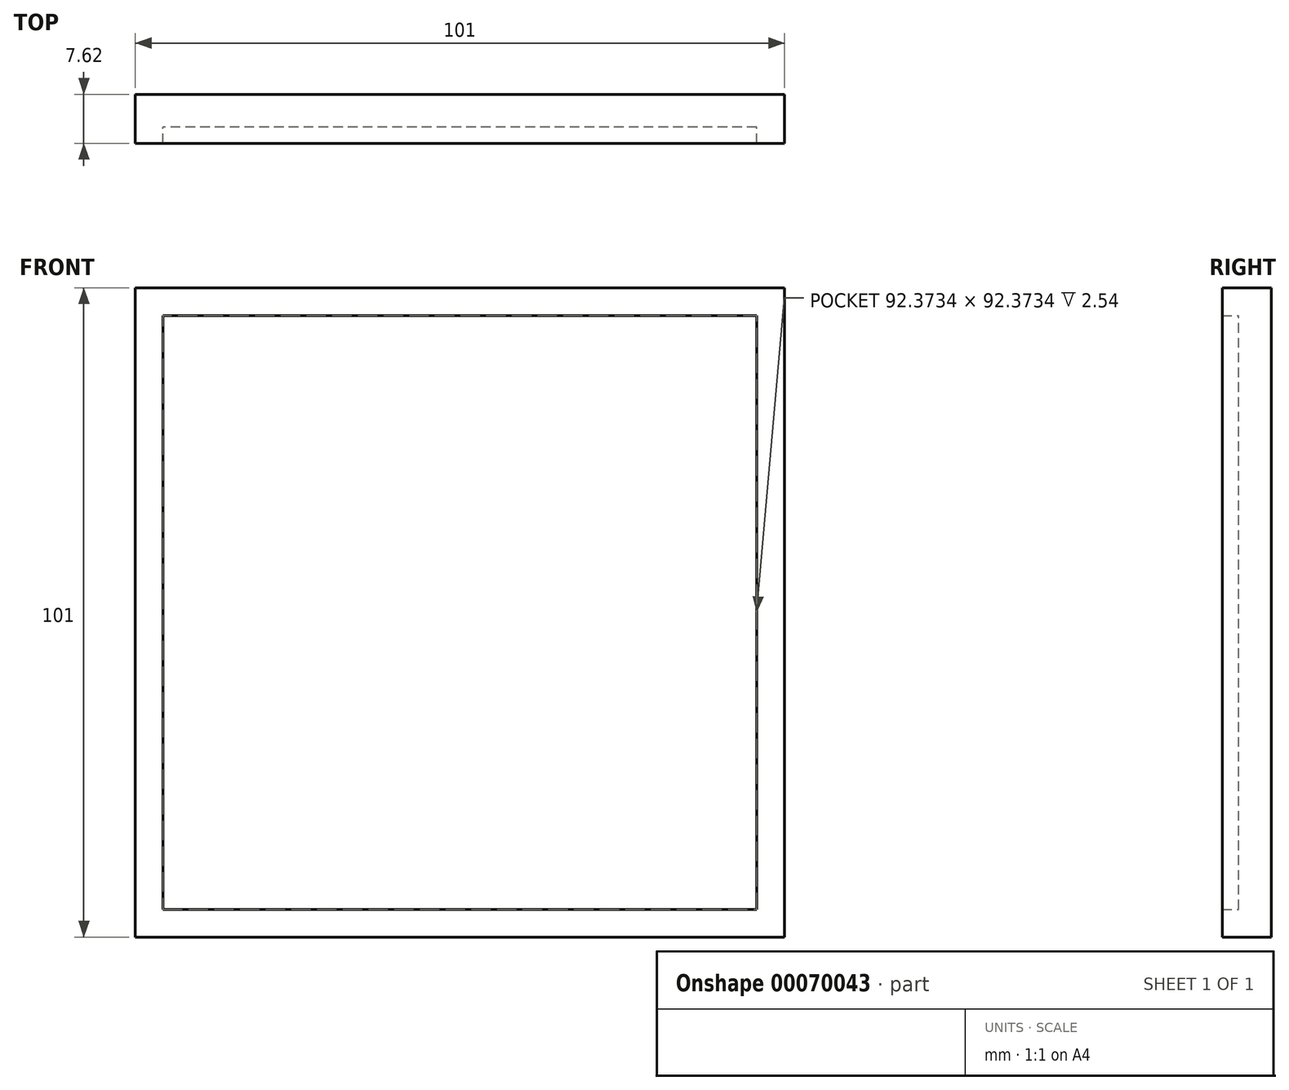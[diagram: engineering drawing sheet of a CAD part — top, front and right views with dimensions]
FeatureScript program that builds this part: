
annotation { "Feature Type Name" : "Feature", "Feature Type Description" : "" }
export const myFeature = defineFeature(function(context is Context, id is Id, definition is map)
    precondition{}
    {
        {
            var Q0;
            Q0=qCreatedBy(makeId("Front.planeOp"),FACE);
            var sketch = newSketch(context, id + "F0", { "sketchPlane" : qUnion([Q0])});
            skLineSegment(sketch, "E0.rect.bottom", {"start": v(50.8, -50.8) * mm, "end": v(-50.8, -50.8) * mm});
            skLineSegment(sketch, "E0.rect.top", {"start": v(50.8, 50.8) * mm, "end": v(-50.8, 50.8) * mm});
            skLineSegment(sketch, "E0.rect.left", {"start": v(50.8, -50.8) * mm, "end": v(50.8, 50.8) * mm});
            skLineSegment(sketch, "E0.rect.right", {"start": v(-50.8, -50.8) * mm, "end": v(-50.8, 50.8) * mm});
            skLineSegment(sketch, "E1.0", {"start": v(50.5, 50.5) * mm, "end": v(-50.5, 50.5) * mm});
            skLineSegment(sketch, "E1.1", {"start": v(50.5, -50.5) * mm, "end": v(50.5, 50.5) * mm});
            skLineSegment(sketch, "E1.2", {"start": v(50.5, -50.5) * mm, "end": v(-50.5, -50.5) * mm});
            skLineSegment(sketch, "E1.3", {"start": v(-50.5, -50.5) * mm, "end": v(-50.5, 50.5) * mm});
            skSolve(sketch);
        }
        {
            var Q0;
            Q0=makeQuery(id+"F0.imprint","IMPRINT",FACE,{"disambiguationData":[TD([[makeQuery(id+"F0.imprint","IMPRINT",EDGE,{"derivedFrom":sQuery(id+"F0.wireOp",EDGE,"E1.0")}),1.0]])]});
            extrude(context, id + "F1", {"entities" : qUnion([Q0]), "depth" : 5.08 * mm});
        }
        {
            var Q0;
            Q0=makeQuery(id+"F1.opExtrude","CAP_FACE",FACE,{"disambiguationData":[OSD([sQuery(id+"F0.wireOp",EDGE,"E1.0"),sQuery(id+"F0.wireOp",EDGE,"E1.1"),sQuery(id+"F0.wireOp",EDGE,"E1.2"),sQuery(id+"F0.wireOp",EDGE,"E1.3")])],"isStart":false});
            var sketch = newSketch(context, id + "F2", { "sketchPlane" : qUnion([Q0])});
            skLineSegment(sketch, "E2.bottom", {"start": v(46.19, -46.19) * mm, "end": v(-46.19, -46.19) * mm});
            skLineSegment(sketch, "E2.top", {"start": v(46.19, 46.19) * mm, "end": v(-46.19, 46.19) * mm});
            skLineSegment(sketch, "E2.left", {"start": v(46.19, -46.19) * mm, "end": v(46.19, 46.19) * mm});
            skLineSegment(sketch, "E2.right", {"start": v(-46.19, -46.19) * mm, "end": v(-46.19, 46.19) * mm});
            skPoint(sketch, "E2.middle", {"position": v(0, 0) * mm});
            skLineSegment(sketch, "E3.bottom", {"start": v(50.5, -50.5) * mm, "end": v(-50.5, -50.5) * mm});
            skLineSegment(sketch, "E3.top", {"start": v(50.5, 50.5) * mm, "end": v(-50.5, 50.5) * mm});
            skLineSegment(sketch, "E3.left", {"start": v(50.5, -50.5) * mm, "end": v(50.5, 50.5) * mm});
            skLineSegment(sketch, "E3.right", {"start": v(-50.5, -50.5) * mm, "end": v(-50.5, 50.5) * mm});
            skSolve(sketch);
        }
        {
            var Q0;
            Q0=makeQuery(id+"F2.imprint","IMPRINT",FACE,{"disambiguationData":[TD([[makeQuery(id+"F2.imprint","IMPRINT",EDGE,{"derivedFrom":sQuery(id+"F2.wireOp",EDGE,"E2.bottom")}),1.0]])]});
            extrude(context, id + "F3", {"entities" : qUnion([Q0]), "operationType" : NewBodyOperationType.ADD, "depth" : 2.54 * mm});
        }
        {
            var Q0;
            Q0=makeQuery(id+"F1.opExtrude","CAP_FACE",FACE,{"disambiguationData":[OSD([sQuery(id+"F0.wireOp",EDGE,"E1.0"),sQuery(id+"F0.wireOp",EDGE,"E1.1"),sQuery(id+"F0.wireOp",EDGE,"E1.2"),sQuery(id+"F0.wireOp",EDGE,"E1.3")])],"isStart":false});
            var sketch = newSketch(context, id + "F4", { "sketchPlane" : qUnion([Q0])});
            skLineSegment(sketch, "E4.bottom", {"start": v(41.1, -41.1) * mm, "end": v(-41.1, -41.1) * mm});
            skLineSegment(sketch, "E4.top", {"start": v(41.1, 41.1) * mm, "end": v(-41.1, 41.1) * mm});
            skLineSegment(sketch, "E4.left", {"start": v(41.1, -41.1) * mm, "end": v(41.1, 41.1) * mm});
            skLineSegment(sketch, "E4.right", {"start": v(-41.1, -41.1) * mm, "end": v(-41.1, 41.1) * mm});
            skPoint(sketch, "E4.middle", {"position": v(0, 0) * mm});
            skCircle(sketch, "E5", {"center": v(-41.1, 41.1) * mm, "radius": 2.54 * mm});
            skCircle(sketch, "E6", {"center": v(-33.49, 41.1) * mm, "radius": 2.54 * mm});
            skCircle(sketch, "E7", {"center": v(-24.36, 41.1) * mm, "radius": 2.54 * mm});
            skCircle(sketch, "E8", {"center": v(-15.97, 41.1) * mm, "radius": 2.54 * mm});
            skCircle(sketch, "E9", {"center": v(-8.8, 41.1) * mm, "radius": 2.54 * mm});
            skCircle(sketch, "E10", {"center": v(0, 41.1) * mm, "radius": 2.54 * mm});
            skSolve(sketch);
        }
        {
            var Q0;
            Q0=sQuery(id+"F4.wireOp",EDGE,"E5");
            extrude(context, id + "F5", {"bodyType" : ToolBodyType.SURFACE, "surfaceEntities" : qUnion([Q0]), "depth" : 2.54 * mm});
        }
    });
